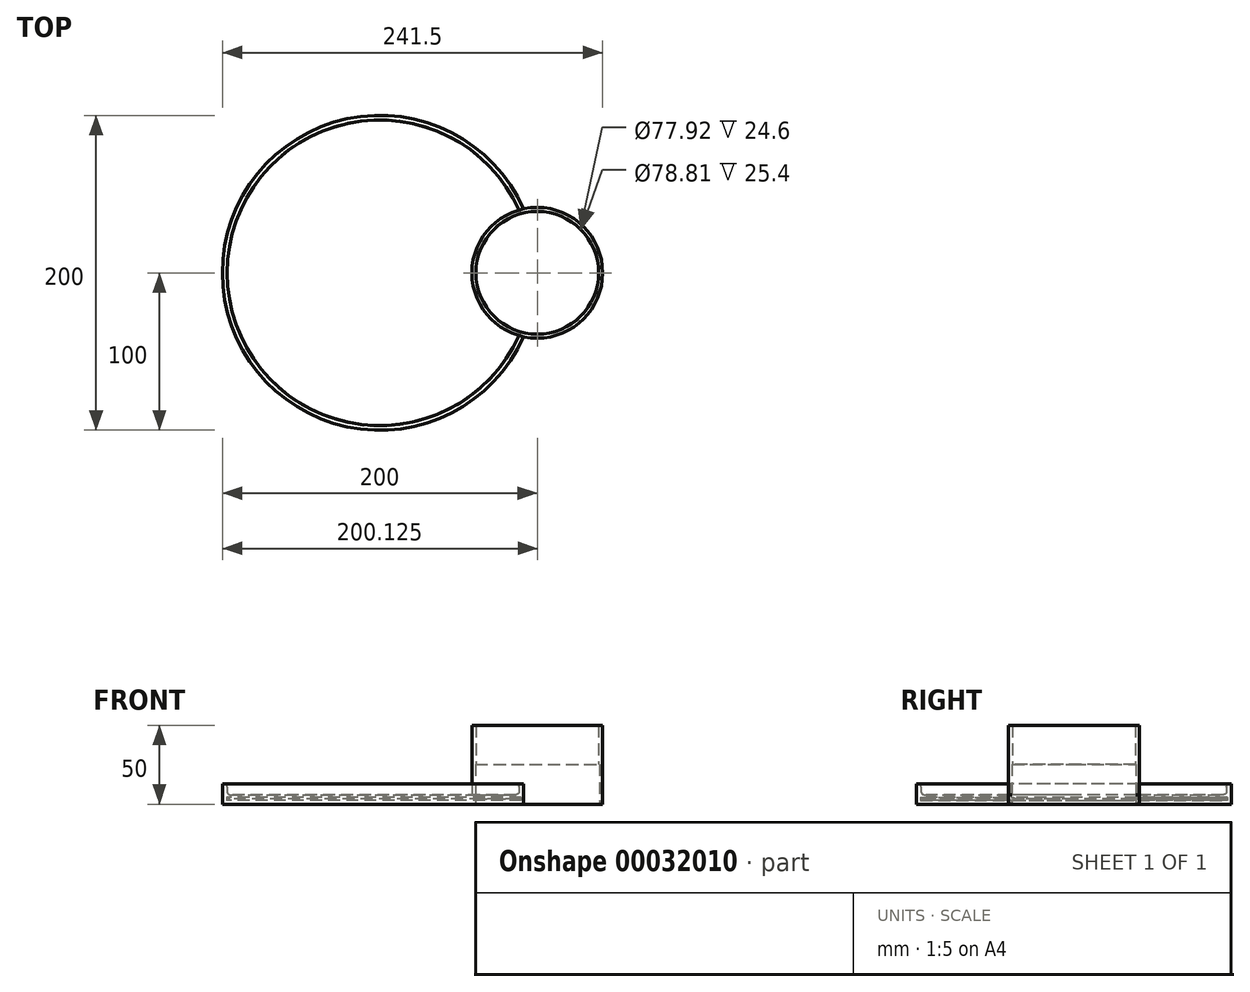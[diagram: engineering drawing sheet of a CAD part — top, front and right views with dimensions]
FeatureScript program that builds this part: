
annotation { "Feature Type Name" : "Feature", "Feature Type Description" : "" }
export const myFeature = defineFeature(function(context is Context, id is Id, definition is map)
    precondition{}
    {
        {
            var Q0;
            Q0=qCreatedBy(makeId("Top.planeOp"),FACE);
            var sketch = newSketch(context, id + "F0", { "sketchPlane" : qUnion([Q0])});
            skCircle(sketch, "E0", {"center": v(0, 0) * mm, "radius": 100 * mm});
            skSolve(sketch);
        }
        {
            var Q0;
            Q0=makeQuery(id+"F0.imprint","IMPRINT",FACE,{"disambiguationData":[TD([[makeQuery(id+"F0.imprint","IMPRINT",EDGE,{"derivedFrom":sQuery(id+"F0.wireOp",EDGE,"E0")}),1.0]])]});
            extrude(context, id + "F1", {"entities" : qUnion([Q0]), "depth" : 10 * mm});
        }
        {
            var Q0;
            Q0=makeQuery(id+"F1.opExtrude","CAP_FACE",FACE,{"disambiguationData":[OSD([sQuery(id+"F0.wireOp",EDGE,"E0")])],"isStart":false});
            shell(context, id + "F2", {"entities" : qUnion([Q0]), "thickness" : 3 * mm});
        }
        {
            var Q0;
            Q0=makeQuery(id+"F1.opExtrude","CAP_FACE",FACE,{"disambiguationData":[OSD([sQuery(id+"F0.wireOp",EDGE,"E0")])],"isStart":true});
            var sketch = newSketch(context, id + "F3", { "sketchPlane" : qUnion([Q0])});
            skCircle(sketch, "E1", {"center": v(0, 0) * mm, "radius": 100 * mm});
            skSolve(sketch);
        }
        {
            var Q0;
            Q0=makeQuery(id+"F3.imprint","IMPRINT",FACE,{"disambiguationData":[TD([[makeQuery(id+"F3.imprint","IMPRINT",EDGE,{"derivedFrom":sQuery(id+"F3.wireOp",EDGE,"E1")}),-1.0]])]});
            extrude(context, id + "F4", {"entities" : qUnion([Q0]), "operationType" : NewBodyOperationType.ADD, "depth" : 3 * mm});
        }
        {
            var Q0;
            {var subQ0=sQuery(id+"F0.wireOp",EDGE,"E0");Q0=makeQuery(id+"F2.opShell","OFFSET_EDGE",EDGE,{"disambiguationData":[OSD([subQ0]),TDD([makeQuery(id+"F1.opExtrude","CAP_EDGE",EDGE,{"disambiguationData":[OSD([subQ0])],"isStart":true})])]});}
            var Q1;
            {var subQ0=sQuery(id+"F0.wireOp",EDGE,"E0");Q1=makeQuery(id+"F2.opShell","OFFSET_EDGE",EDGE,{"disambiguationData":[OSD([subQ0]),TDD([makeQuery(id+"F1.opExtrude","CAP_EDGE",EDGE,{"disambiguationData":[OSD([subQ0])],"isStart":false})])]});}
            fillet(context, id + "F5", {"entities" : qUnion([Q0, Q1]), "radius" : 2 * mm, "tangentPropagation" : true, "allowEdgeOverflow" : false});
        }
        {
            var Q0;
            Q0=makeQuery(id+"F4.opExtrude","CAP_FACE",FACE,{"disambiguationData":[OSD([sQuery(id+"F3.wireOp",EDGE,"E1")])],"isStart":false});
            var sketch = newSketch(context, id + "F6", { "sketchPlane" : qUnion([Q0])});
            skCircle(sketch, "E2", {"center": v(100, 0) * mm, "radius": 41.5 * mm});
            skSolve(sketch);
        }
        {
            var Q0;
            {var subQ0=makeQuery(id+"F4.opExtrude","CAP_EDGE",EDGE,{"disambiguationData":[OSD([sQuery(id+"F3.wireOp",EDGE,"E1")])],"isStart":false});var subQ1=sQuery(id+"F6.wireOp",EDGE,"E2");var subQ3=makeQuery(id+"F6.imprint","INTERSECT",VERTEX,{"disambiguationData":[OD(0.0)],"derivedFrom":[subQ0,subQ1]});Q0=makeQuery(id+"F6.imprint","IMPRINT",FACE,{"disambiguationData":[TD([[makeQuery(id+"F6.imprint","IMPRINT",EDGE,{"disambiguationData":[TD([[subQ3,1.0]])],"derivedFrom":subQ1}),1.0]])]});}
            var Q1;
            {var subQ0=makeQuery(id+"F4.opExtrude","CAP_EDGE",EDGE,{"disambiguationData":[OSD([sQuery(id+"F3.wireOp",EDGE,"E1")])],"isStart":false});var subQ1=sQuery(id+"F6.wireOp",EDGE,"E2");var subQ3=makeQuery(id+"F6.imprint","INTERSECT",VERTEX,{"disambiguationData":[OD(0.0)],"derivedFrom":[subQ0,subQ1]});Q1=makeQuery(id+"F6.imprint","IMPRINT",FACE,{"disambiguationData":[TD([[makeQuery(id+"F6.imprint","IMPRINT",EDGE,{"disambiguationData":[TD([[subQ3,-1.0]])],"derivedFrom":subQ1}),1.0]])]});}
            extrude(context, id + "F7", {"entities" : qUnion([Q0, Q1]), "operationType" : NewBodyOperationType.ADD, "oppositeDirection" : true, "depth" : 50 * mm});
        }
        {
            var Q0;
            Q0=makeQuery(id+"F7.boolean.opBoolean","MERGE",FACE,{"derivedFrom":[makeQuery(id+"F4.opExtrude","CAP_FACE",FACE,{"disambiguationData":[OSD([sQuery(id+"F3.wireOp",EDGE,"E1")])],"isStart":false}),makeQuery(id+"F7.opExtrude","CAP_FACE",FACE,{"disambiguationData":[OSD([sQuery(id+"F6.wireOp",EDGE,"E2")])],"isStart":true})]});
            var sketch = newSketch(context, id + "F8", { "sketchPlane" : qUnion([Q0])});
            skCircle(sketch, "E3", {"center": v(100, 0) * mm, "radius": 41.5 * mm});
            skSolve(sketch);
        }
        {
            var Q0;
            Q0=makeQuery(id+"FzJOr6cFBMo9ukw_1.opExtrude","CAP_FACE",FACE,{"disambiguationData":[OSD([sQuery(id+"F8.wireOp",EDGE,"E3")])],"isStart":false});
            var Q1;
            Q1=makeQuery(id+"F7.opExtrude","CAP_FACE",FACE,{"disambiguationData":[OSD([sQuery(id+"F6.wireOp",EDGE,"E2")])],"isStart":false});
            shell(context, id + "F9", {"entities" : qUnion([Q0, Q1]), "thickness" : 2.54 * mm});
        }
        {
            var Q0;
            {var subQ0=sQuery(id+"F8.wireOp",EDGE,"E3");var subQ1=makeQuery(id+"F4.opExtrude","CAP_EDGE",EDGE,{"disambiguationData":[OSD([sQuery(id+"F3.wireOp",EDGE,"E1")])],"isStart":false});var subQ3=makeQuery(id+"F8.imprint","INTERSECT",VERTEX,{"disambiguationData":[OD(0.0)],"derivedFrom":[subQ1,subQ0]});Q0=makeQuery(id+"F8.imprint","IMPRINT",FACE,{"disambiguationData":[TD([[makeQuery(id+"F8.imprint","IMPRINT",EDGE,{"disambiguationData":[TD([[subQ3,-1.0]])],"derivedFrom":subQ0}),1.0]])]});}
            var sketch = newSketch(context, id + "F10", { "sketchPlane" : qUnion([Q0])});
            skCircle(sketch, "E4", {"center": v(100.12, 0) * mm, "radius": 39.4 * mm});
            skSolve(sketch);
        }
        {
            var Q0;
            Q0=qSketchRegion(id+"F10",true);
            extrude(context, id + "F11", {"entities" : qUnion([Q0]), "operationType" : NewBodyOperationType.REMOVE, "oppositeDirection" : true, "depth" : 25.4 * mm});
        }
    });
